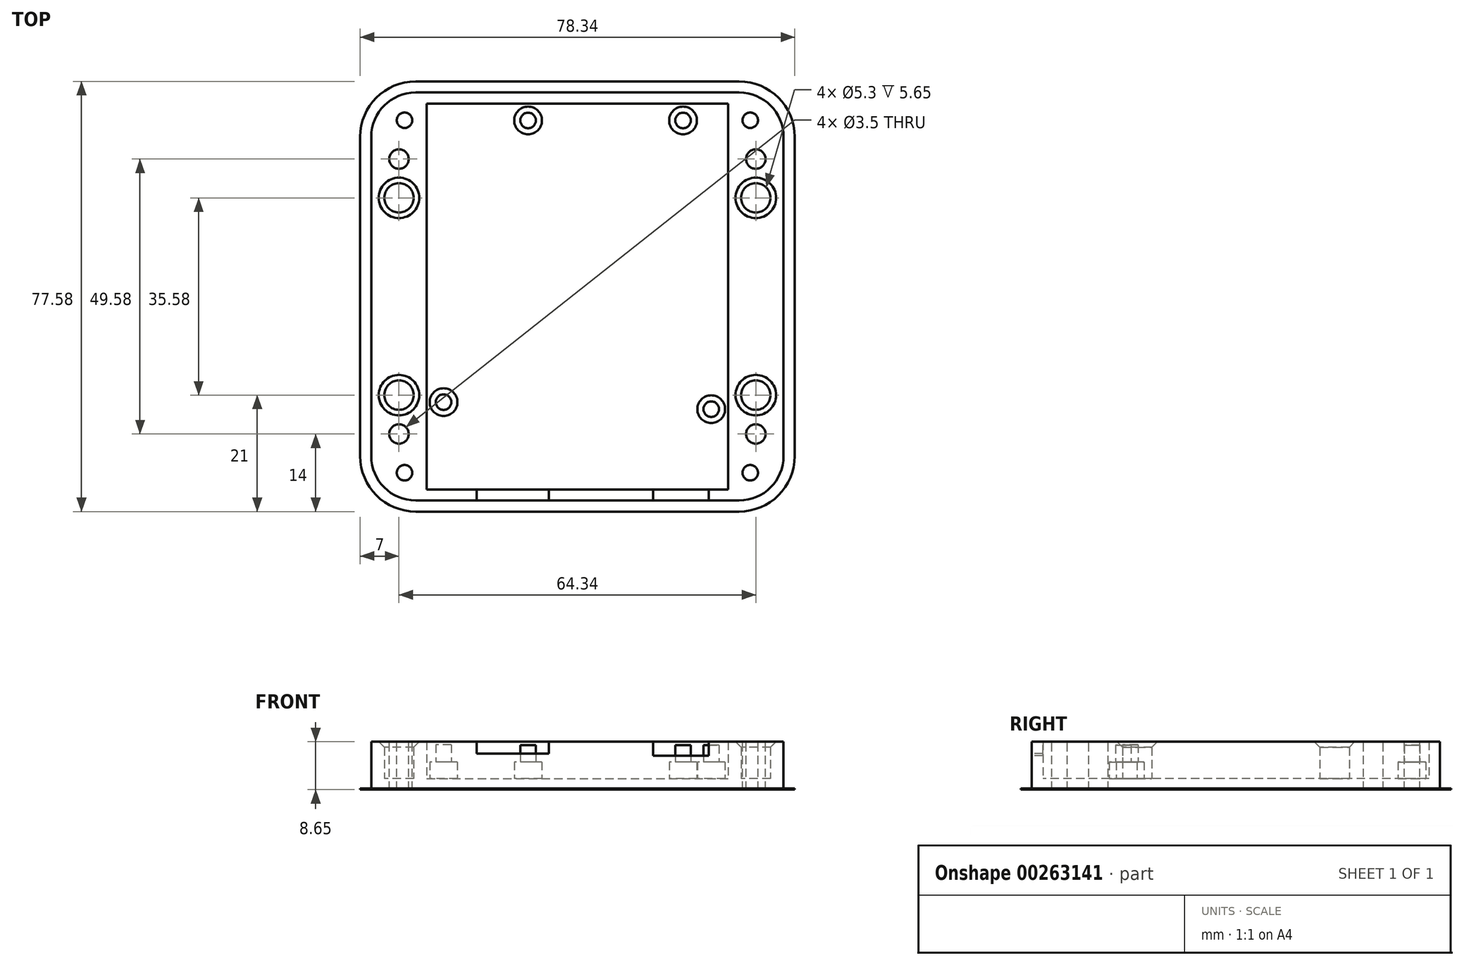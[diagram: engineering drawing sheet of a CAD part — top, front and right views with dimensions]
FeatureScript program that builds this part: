
annotation { "Feature Type Name" : "Feature", "Feature Type Description" : "" }
export const myFeature = defineFeature(function(context is Context, id is Id, definition is map)
    precondition{}
    {
        {
            var Q0;
            Q0=qCreatedBy(makeId("Top.planeOp"),FACE);
            var sketch = newSketch(context, id + "F0", { "sketchPlane" : qUnion([Q0])});
            skLineSegment(sketch, "E0", {"start": v(0, 0) * mm, "end": v(0, 66.04) * mm, "construction": true});
            skLineSegment(sketch, "E1", {"start": v(0, 66.04) * mm, "end": v(12.95, 66.04) * mm, "construction": true});
            skLineSegment(sketch, "E2", {"start": v(12.95, 66.04) * mm, "end": v(15.5, 68.58) * mm, "construction": true});
            skLineSegment(sketch, "E3", {"start": v(15.5, 68.58) * mm, "end": v(48.26, 68.58) * mm, "construction": true});
            skLineSegment(sketch, "E4", {"start": v(48.26, 68.58) * mm, "end": v(50.8, 66.04) * mm, "construction": true});
            skLineSegment(sketch, "E5", {"start": v(50.8, 66.04) * mm, "end": v(53.34, 66.04) * mm, "construction": true});
            skLineSegment(sketch, "E6", {"start": v(53.34, 66.04) * mm, "end": v(53.34, 0) * mm, "construction": true});
            skLineSegment(sketch, "E7", {"start": v(53.34, 0) * mm, "end": v(0, 0) * mm, "construction": true});
            skLineSegment(sketch, "E8", {"start": v(-2.5, 71.08) * mm, "end": v(55.84, 71.08) * mm});
            skLineSegment(sketch, "E9", {"start": v(-2.5, -2.5) * mm, "end": v(55.84, -2.5) * mm});
            skArc(sketch, "E10", {"start": v(63.84, 63.08) * mm, "mid": v(61.5, 68.74) * mm, "end": v(55.84, 71.08) * mm});
            skArc(sketch, "E11", {"start": v(55.84, -2.5) * mm, "mid": v(61.5, -0.16) * mm, "end": v(63.84, 5.5) * mm});
            skLineSegment(sketch, "E12", {"start": v(63.84, 63.08) * mm, "end": v(63.84, 5.5) * mm});
            skArc(sketch, "E13", {"start": v(-10.5, 5.5) * mm, "mid": v(-8.16, -0.16) * mm, "end": v(-2.5, -2.5) * mm});
            skLineSegment(sketch, "E14", {"start": v(-10.5, 63.08) * mm, "end": v(-10.5, 5.5) * mm});
            skArc(sketch, "E15.trimOffspring", {"start": v(-2.5, 71.08) * mm, "mid": v(-8.16, 68.74) * mm, "end": v(-10.5, 63.08) * mm});
            skSolve(sketch);
        }
        {
            var Q0;
            Q0 = qSketchRegion(id + "F0", true);
            extrude(context, id + "F1", {"entities" : qUnion([Q0]), "depth" : 2 * mm});
        }
        {
            var Q0;
            Q0=makeQuery(id+"F1.opExtrude","CAP_FACE",FACE,{"disambiguationData":[OSD([sQuery(id+"F0.wireOp",EDGE,"E8"),sQuery(id+"F0.wireOp",EDGE,"E9"),sQuery(id+"F0.wireOp",EDGE,"E10"),sQuery(id+"F0.wireOp",EDGE,"E11"),sQuery(id+"F0.wireOp",EDGE,"E12"),sQuery(id+"F0.wireOp",EDGE,"E13"),sQuery(id+"F0.wireOp",EDGE,"E14"),sQuery(id+"F0.wireOp",EDGE,"E15.trimOffspring")])],"isStart":false});
            var sketch = newSketch(context, id + "F2", { "sketchPlane" : qUnion([Q0])});
            skLineSegment(sketch, "E16", {"start": v(0, 0) * mm, "end": v(53.34, 0) * mm, "construction": true});
            skLineSegment(sketch, "E17", {"start": v(53.34, 0) * mm, "end": v(53.34, 66.04) * mm, "construction": true});
            skLineSegment(sketch, "E18", {"start": v(53.34, 66.04) * mm, "end": v(50.8, 66.04) * mm, "construction": true});
            skLineSegment(sketch, "E19", {"start": v(50.8, 66.04) * mm, "end": v(48.26, 68.58) * mm, "construction": true});
            skLineSegment(sketch, "E20", {"start": v(48.26, 68.58) * mm, "end": v(15.5, 68.58) * mm, "construction": true});
            skLineSegment(sketch, "E21", {"start": v(15.5, 68.58) * mm, "end": v(12.95, 66.04) * mm, "construction": true});
            skLineSegment(sketch, "E22", {"start": v(12.95, 66.04) * mm, "end": v(0, 66.04) * mm, "construction": true});
            skLineSegment(sketch, "E23", {"start": v(0, 66.04) * mm, "end": v(0, 0) * mm, "construction": true});
            skCircle(sketch, "E24", {"center": v(17.78, 66.04) * mm, "radius": 1.59 * mm, "construction": true});
            skCircle(sketch, "E25", {"center": v(45.72, 66.04) * mm, "radius": 1.59 * mm, "construction": true});
            skCircle(sketch, "E26", {"center": v(2.54, 15.24) * mm, "radius": 1.59 * mm, "construction": true});
            skCircle(sketch, "E27", {"center": v(50.8, 13.97) * mm, "radius": 1.59 * mm, "construction": true});
            skCircle(sketch, "E28", {"center": v(17.78, 66.04) * mm, "radius": 2.5 * mm});
            skCircle(sketch, "E29", {"center": v(45.72, 66.04) * mm, "radius": 2.5 * mm});
            skCircle(sketch, "E30", {"center": v(2.54, 15.24) * mm, "radius": 2.5 * mm});
            skCircle(sketch, "E31", {"center": v(50.8, 13.97) * mm, "radius": 2.5 * mm});
            skSolve(sketch);
        }
        {
            var Q0;
            Q0 = qSketchRegion(id + "F2", true);
            extrude(context, id + "F3", {"entities" : qUnion([Q0]), "operationType" : NewBodyOperationType.ADD, "depth" : 3 * mm});
        }
        {
            var Q0;
            Q0=makeQuery(id+"F3.opExtrude","CAP_FACE",FACE,{"disambiguationData":[OSD([sQuery(id+"F2.wireOp",EDGE,"E28")])],"isStart":false});
            var sketch = newSketch(context, id + "F4", { "sketchPlane" : qUnion([Q0])});
            skCircle(sketch, "E32", {"center": v(17.78, 66.04) * mm, "radius": 1.4 * mm});
            skSolve(sketch);
        }
        {
            var Q0;
            Q0 = qSketchRegion(id + "F4", true);
            extrude(context, id + "F5", {"entities" : qUnion([Q0]), "operationType" : NewBodyOperationType.ADD, "depth" : 3 * mm});
        }
        {
            var Q0;
            Q0=makeQuery(id+"F3.opExtrude","CAP_FACE",FACE,{"disambiguationData":[OSD([sQuery(id+"F2.wireOp",EDGE,"E29")])],"isStart":false});
            var sketch = newSketch(context, id + "F6", { "sketchPlane" : qUnion([Q0])});
            skCircle(sketch, "E33", {"center": v(45.72, 66.04) * mm, "radius": 1.4 * mm});
            skSolve(sketch);
        }
        {
            var Q0;
            Q0 = qSketchRegion(id + "F6", true);
            extrude(context, id + "F7", {"entities" : qUnion([Q0]), "operationType" : NewBodyOperationType.ADD, "depth" : 3 * mm});
        }
        {
            var Q0;
            Q0=makeQuery(id+"F3.opExtrude","CAP_FACE",FACE,{"disambiguationData":[OSD([sQuery(id+"F2.wireOp",EDGE,"E30")])],"isStart":false});
            var sketch = newSketch(context, id + "F8", { "sketchPlane" : qUnion([Q0])});
            skCircle(sketch, "E34", {"center": v(2.54, 15.24) * mm, "radius": 1.4 * mm});
            skSolve(sketch);
        }
        {
            var Q0;
            Q0 = qSketchRegion(id + "F8", true);
            extrude(context, id + "F9", {"entities" : qUnion([Q0]), "operationType" : NewBodyOperationType.ADD, "depth" : 3.1 * mm});
        }
        {
            var Q0;
            Q0=makeQuery(id+"F3.opExtrude","CAP_FACE",FACE,{"disambiguationData":[OSD([sQuery(id+"F2.wireOp",EDGE,"E31")])],"isStart":false});
            var sketch = newSketch(context, id + "F10", { "sketchPlane" : qUnion([Q0])});
            skCircle(sketch, "E35", {"center": v(50.8, 13.97) * mm, "radius": 1.4 * mm});
            skSolve(sketch);
        }
        {
            var Q0;
            Q0 = qSketchRegion(id + "F10", true);
            extrude(context, id + "F11", {"entities" : qUnion([Q0]), "operationType" : NewBodyOperationType.ADD, "depth" : 3 * mm});
        }
        {
            var Q0;
            Q0=makeQuery(id+"F1.opExtrude","CAP_FACE",FACE,{"disambiguationData":[OSD([sQuery(id+"F0.wireOp",EDGE,"E8"),sQuery(id+"F0.wireOp",EDGE,"E9"),sQuery(id+"F0.wireOp",EDGE,"E10"),sQuery(id+"F0.wireOp",EDGE,"E11"),sQuery(id+"F0.wireOp",EDGE,"E12"),sQuery(id+"F0.wireOp",EDGE,"E13"),sQuery(id+"F0.wireOp",EDGE,"E14"),sQuery(id+"F0.wireOp",EDGE,"E15.trimOffspring")])],"isStart":false});
            var sketch = newSketch(context, id + "F12", { "sketchPlane" : qUnion([Q0])});
            skLineSegment(sketch, "E36", {"start": v(-8.5, 55.08) * mm, "end": v(-8.5, 13.5) * mm, "construction": true});
            skLineSegment(sketch, "E37", {"start": v(-10.5, 63.08) * mm, "end": v(-10.5, 5.5) * mm});
            skLineSegment(sketch, "E38", {"start": v(-2.5, -2.5) * mm, "end": v(55.84, -2.5) * mm});
            skLineSegment(sketch, "E39", {"start": v(63.84, 5.5) * mm, "end": v(63.84, 63.08) * mm});
            skLineSegment(sketch, "E40", {"start": v(55.84, 71.08) * mm, "end": v(-2.5, 71.08) * mm});
            skArc(sketch, "E41", {"start": v(-2.5, 71.08) * mm, "mid": v(-8.16, 68.74) * mm, "end": v(-10.5, 63.08) * mm});
            skArc(sketch, "E42", {"start": v(-10.5, 5.5) * mm, "mid": v(-8.16, -0.16) * mm, "end": v(-2.5, -2.5) * mm});
            skArc(sketch, "E43", {"start": v(55.84, -2.5) * mm, "mid": v(61.5, -0.16) * mm, "end": v(63.84, 5.5) * mm});
            skArc(sketch, "E44", {"start": v(63.84, 63.08) * mm, "mid": v(61.5, 68.74) * mm, "end": v(55.84, 71.08) * mm});
            skLineSegment(sketch, "E45", {"start": v(-0.5, 69.08) * mm, "end": v(53.84, 69.08) * mm});
            skLineSegment(sketch, "E46", {"start": v(61.84, 55.08) * mm, "end": v(61.84, 13.5) * mm, "construction": true});
            skLineSegment(sketch, "E47", {"start": v(-0.5, -0.5) * mm, "end": v(53.84, -0.5) * mm});
            skLineSegment(sketch, "E48", {"start": v(-0.5, 69.08) * mm, "end": v(-0.5, -0.5) * mm});
            skLineSegment(sketch, "E49", {"start": v(53.84, 69.08) * mm, "end": v(53.84, -0.5) * mm});
            skCircle(sketch, "E50", {"center": v(-4.5, 66.08) * mm, "radius": 1.4 * mm, "construction": true});
            skCircle(sketch, "E51", {"center": v(-5.5, 59.08) * mm, "radius": 1.75 * mm, "construction": true});
            skLineSegment(sketch, "E52", {"start": v(-8.5, 55.08) * mm, "end": v(-2.5, 55.08) * mm, "construction": true});
            skLineSegment(sketch, "E53.trimOffspring", {"start": v(-2.5, 55.08) * mm, "end": v(-2.5, 13.5) * mm, "construction": true});
            skLineSegment(sketch, "E54", {"start": v(-10.5, 63.08) * mm, "end": v(-0.5, 63.08) * mm, "construction": true});
            skLineSegment(sketch, "E55", {"start": v(55.84, 55.08) * mm, "end": v(61.84, 55.08) * mm, "construction": true});
            skLineSegment(sketch, "E56", {"start": v(63.84, 63.08) * mm, "end": v(53.84, 63.08) * mm, "construction": true});
            skLineSegment(sketch, "E57", {"start": v(-8.5, 13.5) * mm, "end": v(-2.5, 13.5) * mm, "construction": true});
            skPoint(sketch, "E58.end.orphan", {"position": v(-2.5, -0.5) * mm});
            skLineSegment(sketch, "E59", {"start": v(-10.5, 5.5) * mm, "end": v(-0.5, 5.5) * mm, "construction": true});
            skCircle(sketch, "E60", {"center": v(57.84, 66.08) * mm, "radius": 1.4 * mm, "construction": true});
            skCircle(sketch, "E61", {"center": v(58.84, 59.08) * mm, "radius": 1.75 * mm, "construction": true});
            skCircle(sketch, "E62", {"center": v(-5.5, 9.5) * mm, "radius": 1.75 * mm, "construction": true});
            skCircle(sketch, "E63", {"center": v(-4.5, 2.5) * mm, "radius": 1.4 * mm, "construction": true});
            skLineSegment(sketch, "E64", {"start": v(55.84, 13.5) * mm, "end": v(61.84, 13.5) * mm, "construction": true});
            skLineSegment(sketch, "E65", {"start": v(63.84, 5.5) * mm, "end": v(53.84, 5.5) * mm, "construction": true});
            skLineSegment(sketch, "E66", {"start": v(55.84, 55.08) * mm, "end": v(55.84, 13.5) * mm, "construction": true});
            skCircle(sketch, "E67", {"center": v(57.84, 2.5) * mm, "radius": 1.4 * mm, "construction": true});
            skCircle(sketch, "E68", {"center": v(58.84, 9.5) * mm, "radius": 1.75 * mm, "construction": true});
            skCircle(sketch, "E69", {"center": v(-5.5, 52.08) * mm, "radius": 2.65 * mm});
            skCircle(sketch, "E70", {"center": v(-5.5, 16.5) * mm, "radius": 2.65 * mm});
            skCircle(sketch, "E71", {"center": v(58.84, 52.08) * mm, "radius": 2.65 * mm});
            skCircle(sketch, "E72", {"center": v(58.84, 16.5) * mm, "radius": 2.65 * mm});
            skSolve(sketch);
        }
        {
            var Q0;
            Q0 = qSketchRegion(id + "F12", true);
            extrude(context, id + "F13", {"entities" : qUnion([Q0]), "operationType" : NewBodyOperationType.ADD, "depth" : 6.65 * mm});
        }
        {
            var Q0;
            Q0=makeQuery(id+"F13.opExtrude","CAP_FACE",FACE,{"disambiguationData":[OSD([sQuery(id+"F12.wireOp",EDGE,"E36"),sQuery(id+"F12.wireOp",EDGE,"E37"),sQuery(id+"F12.wireOp",EDGE,"E38"),sQuery(id+"F12.wireOp",EDGE,"E39"),sQuery(id+"F12.wireOp",EDGE,"E40"),sQuery(id+"F12.wireOp",EDGE,"E41"),sQuery(id+"F12.wireOp",EDGE,"E42"),sQuery(id+"F12.wireOp",EDGE,"E43"),sQuery(id+"F12.wireOp",EDGE,"E44"),sQuery(id+"F12.wireOp",EDGE,"E45"),sQuery(id+"F12.wireOp",EDGE,"E46"),sQuery(id+"F12.wireOp",EDGE,"E47"),sQuery(id+"F12.wireOp",EDGE,"E48"),sQuery(id+"F12.wireOp",EDGE,"E49"),sQuery(id+"F12.wireOp",EDGE,"E52"),sQuery(id+"F12.wireOp",EDGE,"E53.trimOffspring"),sQuery(id+"F12.wireOp",EDGE,"E55"),sQuery(id+"F12.wireOp",EDGE,"E57"),sQuery(id+"F12.wireOp",EDGE,"E64"),sQuery(id+"F12.wireOp",EDGE,"E66")])],"isStart":false});
            var sketch = newSketch(context, id + "F14", { "sketchPlane" : qUnion([Q0])});
            skLineSegment(sketch, "E73", {"start": v(-10.5, 5.5) * mm, "end": v(-0.5, 5.5) * mm, "construction": true});
            skCircle(sketch, "E74", {"center": v(-5.5, 9.5) * mm, "radius": 1.75 * mm});
            skCircle(sketch, "E75", {"center": v(-4.5, 2.5) * mm, "radius": 1.4 * mm});
            skLineSegment(sketch, "E76", {"start": v(63.84, 5.5) * mm, "end": v(53.84, 5.5) * mm, "construction": true});
            skLineSegment(sketch, "E77", {"start": v(-10.5, 63.08) * mm, "end": v(-0.5, 63.08) * mm, "construction": true});
            skLineSegment(sketch, "E78", {"start": v(63.84, 63.08) * mm, "end": v(53.84, 63.08) * mm, "construction": true});
            skCircle(sketch, "E79", {"center": v(-4.5, 66.08) * mm, "radius": 1.4 * mm});
            skCircle(sketch, "E80", {"center": v(-5.5, 59.08) * mm, "radius": 1.75 * mm});
            skCircle(sketch, "E81", {"center": v(57.84, 66.08) * mm, "radius": 1.4 * mm});
            skCircle(sketch, "E82", {"center": v(58.84, 59.08) * mm, "radius": 1.75 * mm});
            skCircle(sketch, "E83", {"center": v(58.84, 9.5) * mm, "radius": 1.75 * mm});
            skCircle(sketch, "E84", {"center": v(57.84, 2.5) * mm, "radius": 1.4 * mm});
            skSolve(sketch);
        }
        {
            var Q0;
            Q0 = qSketchRegion(id + "F14", true);
            extrude(context, id + "F15", {"entities" : qUnion([Q0]), "operationType" : NewBodyOperationType.REMOVE, "oppositeDirection" : true, "depth" : 25 * mm});
        }
        {
            var Q0;
            Q0=makeQuery(id+"F13.boolean.opBoolean","MERGE",FACE,{"derivedFrom":[makeQuery(id+"F1.opExtrude","SWEPT_FACE",FACE,{"disambiguationData":[OSD([sQuery(id+"F0.wireOp",EDGE,"E9")])]}),makeQuery(id+"F13.opExtrude","SWEPT_FACE",FACE,{"disambiguationData":[OSD([sQuery(id+"F12.wireOp",EDGE,"E38")])]})]});
            var sketch = newSketch(context, id + "F16", { "sketchPlane" : qUnion([Q0])});
            skLineSegment(sketch, "E85.bottom", {"start": v(8.5, 8.65) * mm, "end": v(21.54, 8.65) * mm});
            skLineSegment(sketch, "E85.top", {"start": v(8.5, 6.52) * mm, "end": v(21.54, 6.52) * mm});
            skLineSegment(sketch, "E85.left", {"start": v(8.5, 8.65) * mm, "end": v(8.5, 6.52) * mm});
            skLineSegment(sketch, "E85.right", {"start": v(21.54, 8.65) * mm, "end": v(21.54, 6.52) * mm});
            skLineSegment(sketch, "E86.bottom", {"start": v(40.34, 8.65) * mm, "end": v(50.34, 8.65) * mm});
            skLineSegment(sketch, "E86.top", {"start": v(40.34, 6.15) * mm, "end": v(50.34, 6.15) * mm});
            skLineSegment(sketch, "E86.left", {"start": v(40.34, 8.65) * mm, "end": v(40.34, 6.15) * mm});
            skLineSegment(sketch, "E86.right", {"start": v(50.34, 8.65) * mm, "end": v(50.34, 6.15) * mm});
            skSolve(sketch);
        }
        {
            var Q0;
            Q0 = qSketchRegion(id + "F16", true);
            extrude(context, id + "F17", {"entities" : qUnion([Q0]), "operationType" : NewBodyOperationType.REMOVE, "oppositeDirection" : true, "depth" : 3 * mm});
        }
        {
            var Q0;
            Q0=makeQuery(id+"F13.opExtrude","CAP_EDGE",EDGE,{"disambiguationData":[OSD([sQuery(id+"F12.wireOp",EDGE,"E72")])],"isStart":false});
            var Q1;
            Q1=makeQuery(id+"F13.opExtrude","CAP_EDGE",EDGE,{"disambiguationData":[OSD([sQuery(id+"F12.wireOp",EDGE,"E71")])],"isStart":false});
            var Q2;
            Q2=makeQuery(id+"F13.opExtrude","CAP_EDGE",EDGE,{"disambiguationData":[OSD([sQuery(id+"F12.wireOp",EDGE,"E69")])],"isStart":false});
            var Q3;
            Q3=makeQuery(id+"F13.opExtrude","CAP_EDGE",EDGE,{"disambiguationData":[OSD([sQuery(id+"F12.wireOp",EDGE,"E70")])],"isStart":false});
            chamfer(context, id + "F18", {"entities" : qUnion([Q0, Q1, Q2, Q3]), "width" : 1 * mm, "tangentPropagation" : true});
        }
        {
            var Q0;
            Q0=makeQuery(id+"F1.opExtrude","CAP_FACE",FACE,{"disambiguationData":[OSD([sQuery(id+"F0.wireOp",EDGE,"E8"),sQuery(id+"F0.wireOp",EDGE,"E9"),sQuery(id+"F0.wireOp",EDGE,"E10"),sQuery(id+"F0.wireOp",EDGE,"E11"),sQuery(id+"F0.wireOp",EDGE,"E12"),sQuery(id+"F0.wireOp",EDGE,"E13"),sQuery(id+"F0.wireOp",EDGE,"E14"),sQuery(id+"F0.wireOp",EDGE,"E15.trimOffspring")])],"isStart":true});
            var sketch = newSketch(context, id + "F19", { "sketchPlane" : qUnion([Q0])});
            skLineSegment(sketch, "E87", {"start": v(-10.5, -5.5) * mm, "end": v(-10.5, -63.08) * mm});
            skLineSegment(sketch, "E88", {"start": v(-2.5, 2.5) * mm, "end": v(55.84, 2.5) * mm});
            skLineSegment(sketch, "E89", {"start": v(63.84, -5.5) * mm, "end": v(63.84, -63.08) * mm});
            skLineSegment(sketch, "E90", {"start": v(-2.5, -71.08) * mm, "end": v(55.84, -71.08) * mm});
            skArc(sketch, "E91", {"start": v(-2.5, 2.5) * mm, "mid": v(-8.16, 0.16) * mm, "end": v(-10.5, -5.5) * mm});
            skArc(sketch, "E92", {"start": v(63.84, -5.5) * mm, "mid": v(61.5, 0.16) * mm, "end": v(55.84, 2.5) * mm});
            skArc(sketch, "E93", {"start": v(-10.5, -63.08) * mm, "mid": v(-8.16, -68.74) * mm, "end": v(-2.5, -71.08) * mm});
            skArc(sketch, "E94", {"start": v(55.84, -71.08) * mm, "mid": v(61.5, -68.74) * mm, "end": v(63.84, -63.08) * mm});
            skLineSegment(sketch, "E95", {"start": v(-12.5, -5.5) * mm, "end": v(-12.5, -63.08) * mm});
            skLineSegment(sketch, "E96", {"start": v(-2.5, 4.5) * mm, "end": v(55.84, 4.5) * mm});
            skLineSegment(sketch, "E97", {"start": v(65.84, -5.5) * mm, "end": v(65.84, -63.08) * mm});
            skLineSegment(sketch, "E98", {"start": v(-2.5, -73.08) * mm, "end": v(55.84, -73.08) * mm});
            skArc(sketch, "E99", {"start": v(-2.5, 4.5) * mm, "mid": v(-9.57, 1.57) * mm, "end": v(-12.5, -5.5) * mm});
            skArc(sketch, "E100", {"start": v(65.84, -5.5) * mm, "mid": v(62.91, 1.57) * mm, "end": v(55.84, 4.5) * mm});
            skArc(sketch, "E101", {"start": v(-12.5, -63.08) * mm, "mid": v(-9.57, -70.15) * mm, "end": v(-2.5, -73.08) * mm});
            skArc(sketch, "E102", {"start": v(55.84, -73.08) * mm, "mid": v(62.91, -70.15) * mm, "end": v(65.84, -63.08) * mm});
            skSolve(sketch);
        }
        {
            var Q0;
            Q0 = qSketchRegion(id + "F19", true);
            extrude(context, id + "F20", {"entities" : qUnion([Q0]), "operationType" : NewBodyOperationType.ADD, "oppositeDirection" : true, "depth" : 0.2 * mm});
        }
    });
